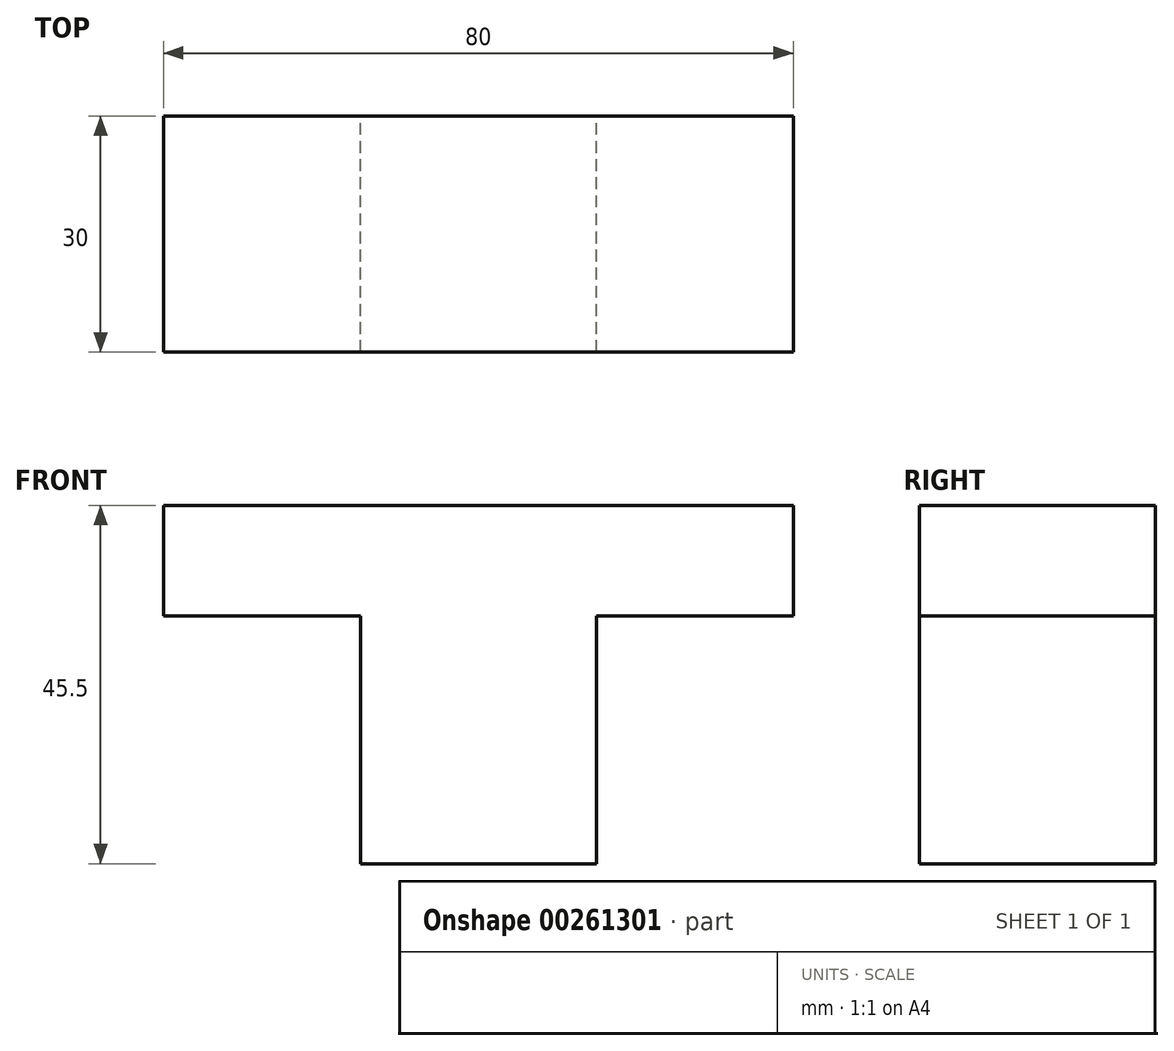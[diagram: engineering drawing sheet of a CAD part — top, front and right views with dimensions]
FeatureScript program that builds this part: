
annotation { "Feature Type Name" : "Feature", "Feature Type Description" : "" }
export const myFeature = defineFeature(function(context is Context, id is Id, definition is map)
    precondition{}
    {
        {
            var Q0;
            Q0=qCreatedBy(makeId("Front.planeOp"),FACE);
            var sketch = newSketch(context, id + "F0", { "sketchPlane" : qUnion([Q0])});
            skLineSegment(sketch, "E0", {"start": v(0, 0) * mm, "end": v(-40, 0) * mm});
            skLineSegment(sketch, "E1", {"start": v(-40, 0) * mm, "end": v(-40, -14) * mm});
            skLineSegment(sketch, "E2", {"start": v(-40, -14) * mm, "end": v(-15, -14) * mm});
            skLineSegment(sketch, "E3", {"start": v(-15, -14) * mm, "end": v(-15, -45.5) * mm});
            skLineSegment(sketch, "E4", {"start": v(-15, -45.5) * mm, "end": v(15, -45.5) * mm});
            skLineSegment(sketch, "E5", {"start": v(15, -45.5) * mm, "end": v(15, -14) * mm});
            skLineSegment(sketch, "E6", {"start": v(15, -14) * mm, "end": v(40, -14) * mm});
            skLineSegment(sketch, "E7", {"start": v(40, -14) * mm, "end": v(40, 0) * mm});
            skLineSegment(sketch, "E8", {"start": v(40, 0) * mm, "end": v(0, 0) * mm});
            skSolve(sketch);
        }
        {
            var Q0;
            Q0 = qSketchRegion(id + "F0", true);
            extrude(context, id + "F1", {"entities" : qUnion([Q0]), "depth" : 30 * mm});
        }
    });
